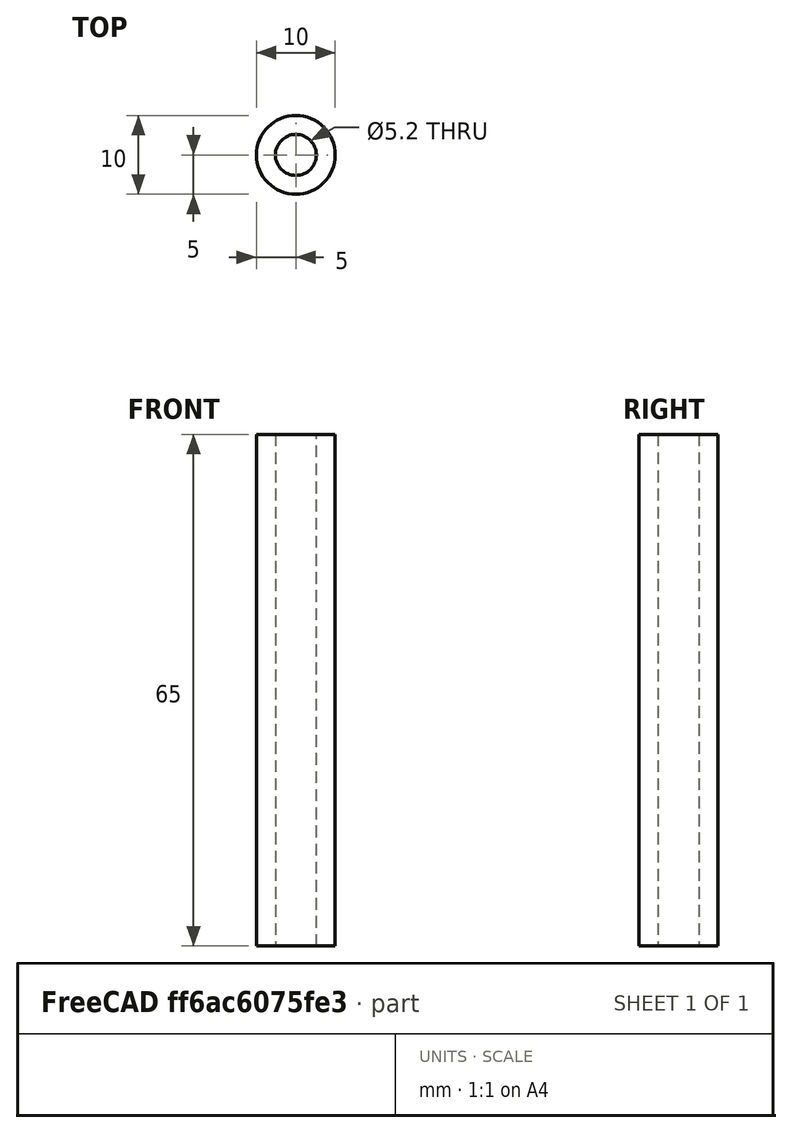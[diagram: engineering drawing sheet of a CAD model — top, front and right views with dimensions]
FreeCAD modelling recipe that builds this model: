
FCSTD DOCUMENT  (FreeCAD 0.21R33771 (Git))
Label: 10D0-5F2-L65
License: All rights reserved
LicenseURL: https://en.wikipedia.org/wiki/All_rights_reserved
objects: Sketcher::SketchObject×1, PartDesign::Pad×1, PartDesign::Body×1
note: 4 computed .brp shape members not serialized (recipe doc carries the construction recipe); baked Part::Feature solids carry a one-line shape summary decoded from their .brp

FEATURE [Sketcher::SketchObject] Sketch
  FullyConstrained = true
  MapMode = 5
  Support = -> [XY_Plane]
  sketch-geometry (6):
    g0: LineSegment StartX=-10 StartY=10 StartZ=0 EndX=10 EndY=10 EndZ=0
    g1: LineSegment StartX=10 StartY=10 StartZ=0 EndX=10 EndY=-10 EndZ=0
    g2: LineSegment StartX=10 StartY=-10 StartZ=0 EndX=-10 EndY=-10 EndZ=0
    g3: LineSegment StartX=-10 StartY=-10 StartZ=0 EndX=-10 EndY=10 EndZ=0
    g4: Circle CenterX=0 CenterY=0 CenterZ=0 NormalX=0 NormalY=0 NormalZ=1 AngleXU=0 Radius=2.6
    g5: Circle CenterX=0 CenterY=0 CenterZ=0 NormalX=0 NormalY=0 NormalZ=1 AngleXU=0 Radius=5
  constraints (14):
    c: Coincident(g0,g1)
    c: Coincident(g1,g2)
    c: Coincident(g2,g3)
    c: Coincident(g3,g0)
    c: Horizontal(g2)
    c: Vertical(g1)
    c: Symmetric(g0,g2,g-1)
    c: Symmetric(g0,g0,g-2)
    c: Equal(g3,g0)
    c: DistanceX(g0,g0) = 20
    c: Coincident(g4,g-1)
    c: Diameter(g4) = 5.2
    c: Coincident(g5,g4)
    c: Diameter(g5) = 10
FEATURE [PartDesign::Pad] Pad
  Direction = (0,0,1)
  Length = 65
  Length2 = 10
  Profile = -> Sketch
  ReferenceAxis = -> Sketch [N_Axis]
  Type = 0
FEATURE [PartDesign::Body] Body
  Group = -> [Sketch,Pad]
  Origin = -> Origin
  Tip = -> Pad
